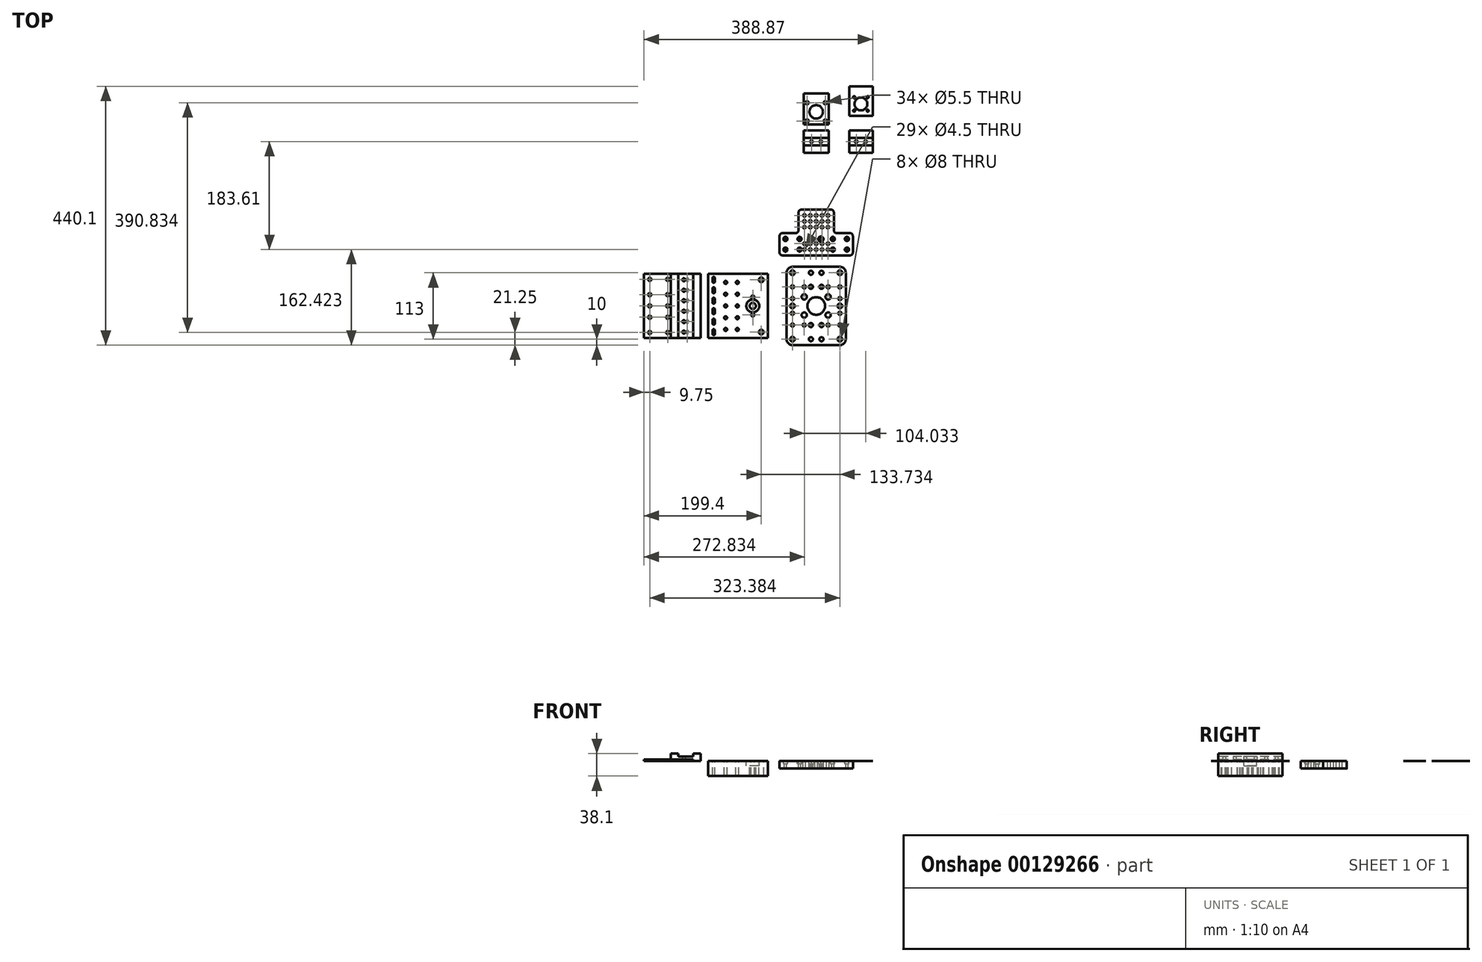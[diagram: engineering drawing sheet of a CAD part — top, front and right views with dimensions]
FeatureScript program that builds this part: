
annotation { "Feature Type Name" : "Feature", "Feature Type Description" : "" }
export const myFeature = defineFeature(function(context is Context, id is Id, definition is map)
    precondition{}
    {
        {
            var Q0;
            Q0=qCreatedBy(makeId("Top.planeOp"),FACE);
            var sketch = newSketch(context, id + "F0", { "sketchPlane" : qUnion([Q0])});
            skLineSegment(sketch, "E0.bottom", {"start": v(0, 0) * mm, "end": v(101.6, 0) * mm});
            skLineSegment(sketch, "E0.top", {"start": v(0, 109) * mm, "end": v(101.6, 109) * mm});
            skLineSegment(sketch, "E0.left", {"start": v(0, 0) * mm, "end": v(0, 109) * mm});
            skLineSegment(sketch, "E0.right", {"start": v(101.6, 0) * mm, "end": v(101.6, 109) * mm});
            skLineSegment(sketch, "E1", {"start": v(9.74, 0) * mm, "end": v(9.74, 109) * mm, "construction": true});
            skLineSegment(sketch, "E2", {"start": v(0, 10) * mm, "end": v(9.74, 10) * mm, "construction": true});
            skLineSegment(sketch, "E3.0.1.0", {"start": v(0, 27.8) * mm, "end": v(9.74, 27.8) * mm, "construction": true});
            skLineSegment(sketch, "E3.0.2.0", {"start": v(0, 45.6) * mm, "end": v(9.74, 45.6) * mm, "construction": true});
            skLineSegment(sketch, "E3.0.3.0", {"start": v(0, 63.4) * mm, "end": v(9.74, 63.4) * mm, "construction": true});
            skLineSegment(sketch, "E3.0.4.0", {"start": v(0, 81.2) * mm, "end": v(9.74, 81.2) * mm, "construction": true});
            skLineSegment(sketch, "E3.0.5.0", {"start": v(0, 99) * mm, "end": v(9.74, 99) * mm, "construction": true});
            skLineSegment(sketch, "E3.direction2", {"start": v(0, 10) * mm, "end": v(0, 27.8) * mm, "construction": true});
            skArc(sketch, "E4", {"start": v(11.74, 30.8) * mm, "mid": v(9.74, 32.8) * mm, "end": v(7.74, 30.8) * mm});
            skLineSegment(sketch, "E5", {"start": v(9.74, 30.8) * mm, "end": v(9.74, 24.8) * mm, "construction": true});
            skArc(sketch, "E6", {"start": v(7.74, 24.8) * mm, "mid": v(9.74, 22.8) * mm, "end": v(11.74, 24.8) * mm});
            skLineSegment(sketch, "E7", {"start": v(11.74, 30.8) * mm, "end": v(11.74, 24.8) * mm});
            skLineSegment(sketch, "E8", {"start": v(7.74, 24.8) * mm, "end": v(7.74, 30.8) * mm});
            skPoint(sketch, "E9", {"position": v(9.74, 27.8) * mm});
            skArc(sketch, "E10", {"start": v(11.74, 48.6) * mm, "mid": v(9.74, 50.6) * mm, "end": v(7.74, 48.6) * mm});
            skLineSegment(sketch, "E11", {"start": v(9.74, 48.6) * mm, "end": v(9.74, 42.6) * mm, "construction": true});
            skArc(sketch, "E12", {"start": v(7.74, 42.6) * mm, "mid": v(9.74, 40.6) * mm, "end": v(11.74, 42.6) * mm});
            skLineSegment(sketch, "E13", {"start": v(11.74, 48.6) * mm, "end": v(11.74, 42.6) * mm});
            skLineSegment(sketch, "E14", {"start": v(7.74, 42.6) * mm, "end": v(7.74, 48.6) * mm});
            skPoint(sketch, "E15", {"position": v(9.74, 45.6) * mm});
            skArc(sketch, "E16", {"start": v(11.74, 102) * mm, "mid": v(9.74, 104) * mm, "end": v(7.74, 102) * mm});
            skLineSegment(sketch, "E17", {"start": v(9.74, 102) * mm, "end": v(9.74, 96) * mm, "construction": true});
            skArc(sketch, "E18", {"start": v(7.74, 96) * mm, "mid": v(9.74, 94) * mm, "end": v(11.74, 96) * mm});
            skLineSegment(sketch, "E19", {"start": v(11.74, 102) * mm, "end": v(11.74, 96) * mm});
            skLineSegment(sketch, "E20", {"start": v(7.74, 96) * mm, "end": v(7.74, 102) * mm});
            skPoint(sketch, "E21", {"position": v(9.74, 99) * mm});
            skArc(sketch, "E22", {"start": v(11.74, 13) * mm, "mid": v(9.74, 15) * mm, "end": v(7.74, 13) * mm});
            skLineSegment(sketch, "E23", {"start": v(9.74, 13) * mm, "end": v(9.74, 7) * mm, "construction": true});
            skArc(sketch, "E24", {"start": v(7.74, 7) * mm, "mid": v(9.74, 5) * mm, "end": v(11.74, 7) * mm});
            skLineSegment(sketch, "E25", {"start": v(11.74, 13) * mm, "end": v(11.74, 7) * mm});
            skLineSegment(sketch, "E26", {"start": v(7.74, 7) * mm, "end": v(7.74, 13) * mm});
            skPoint(sketch, "E27", {"position": v(9.74, 10) * mm});
            skArc(sketch, "E28", {"start": v(11.74, 84.2) * mm, "mid": v(9.74, 86.2) * mm, "end": v(7.74, 84.2) * mm});
            skLineSegment(sketch, "E29", {"start": v(9.74, 84.2) * mm, "end": v(9.74, 78.2) * mm, "construction": true});
            skArc(sketch, "E30", {"start": v(7.74, 78.2) * mm, "mid": v(9.74, 76.2) * mm, "end": v(11.74, 78.2) * mm});
            skLineSegment(sketch, "E31", {"start": v(11.74, 84.2) * mm, "end": v(11.74, 78.2) * mm});
            skLineSegment(sketch, "E32", {"start": v(7.74, 78.2) * mm, "end": v(7.74, 84.2) * mm});
            skPoint(sketch, "E33", {"position": v(9.74, 81.2) * mm});
            skArc(sketch, "E34", {"start": v(11.74, 66.4) * mm, "mid": v(9.74, 68.4) * mm, "end": v(7.74, 66.4) * mm});
            skLineSegment(sketch, "E35", {"start": v(9.74, 66.4) * mm, "end": v(9.74, 60.4) * mm, "construction": true});
            skArc(sketch, "E36", {"start": v(7.74, 60.4) * mm, "mid": v(9.74, 58.4) * mm, "end": v(11.74, 60.4) * mm});
            skLineSegment(sketch, "E37", {"start": v(11.74, 66.4) * mm, "end": v(11.74, 60.4) * mm});
            skLineSegment(sketch, "E38", {"start": v(7.74, 60.4) * mm, "end": v(7.74, 66.4) * mm});
            skPoint(sketch, "E39", {"position": v(9.74, 63.4) * mm});
            skLineSegment(sketch, "E40", {"start": v(76.2, 109) * mm, "end": v(76.2, 0) * mm, "construction": true});
            skPoint(sketch, "E41", {"position": v(76.2, 69.5) * mm});
            skPoint(sketch, "E42", {"position": v(76.2, 54.5) * mm});
            skPoint(sketch, "E43", {"position": v(76.2, 39.5) * mm});
            skCircle(sketch, "E44", {"center": v(76.2, 69.5) * mm, "radius": 2.75 * mm});
            skCircle(sketch, "E45", {"center": v(76.2, 39.5) * mm, "radius": 2.75 * mm});
            skCircle(sketch, "E46", {"center": v(76.2, 54.5) * mm, "radius": 11 * mm});
            skCircle(sketch, "E47", {"center": v(76.2, 54.5) * mm, "radius": 5.26 * mm});
            skLineSegment(sketch, "E48", {"start": v(122.66, 27) * mm, "end": v(122.66, -7) * mm, "construction": true});
            skLineSegment(sketch, "E49", {"start": v(90.6, 10) * mm, "end": v(122.66, 10) * mm, "construction": true});
            skPoint(sketch, "E50", {"position": v(122.66, 10) * mm});
            skLineSegment(sketch, "E51", {"start": v(90.6, 99) * mm, "end": v(122.66, 99) * mm, "construction": true});
            skLineSegment(sketch, "E52", {"start": v(122.66, 116) * mm, "end": v(122.66, 82) * mm, "construction": true});
            skPoint(sketch, "E53", {"position": v(122.66, 99) * mm});
            skLineSegment(sketch, "E54", {"start": v(122.66, 54.5) * mm, "end": v(76.2, 54.5) * mm, "construction": true});
            skLineSegment(sketch, "E55", {"start": v(122.66, 74.5) * mm, "end": v(122.66, 34.5) * mm, "construction": true});
            skPoint(sketch, "E56", {"position": v(122.66, 54.5) * mm});
            skLineSegment(sketch, "E57", {"start": v(90.6, 109) * mm, "end": v(90.6, 0) * mm, "construction": true});
            skPoint(sketch, "E58", {"position": v(90.6, 99) * mm});
            skPoint(sketch, "E59", {"position": v(90.6, 10) * mm});
            skLineSegment(sketch, "E60", {"start": v(122.66, 82) * mm, "end": v(122.66, 74.5) * mm, "construction": true});
            skLineSegment(sketch, "E61", {"start": v(122.66, 34.5) * mm, "end": v(122.66, 27) * mm, "construction": true});
            skCircle(sketch, "E62", {"center": v(90.6, 99) * mm, "radius": 4 * mm});
            skCircle(sketch, "E63", {"center": v(90.6, 10) * mm, "radius": 4 * mm});
            skLineSegment(sketch, "E64", {"start": v(30, 109) * mm, "end": v(30, 0) * mm, "construction": true});
            skLineSegment(sketch, "E65", {"start": v(50, 109) * mm, "end": v(50, 0) * mm, "construction": true});
            skLineSegment(sketch, "E66", {"start": v(50, 54.5) * mm, "end": v(30, 54.5) * mm, "construction": true});
            skLineSegment(sketch, "E67", {"start": v(30, 74.5) * mm, "end": v(50, 74.5) * mm, "construction": true});
            skLineSegment(sketch, "E68", {"start": v(50, 94.5) * mm, "end": v(30, 94.5) * mm, "construction": true});
            skLineSegment(sketch, "E69", {"start": v(30, 34.5) * mm, "end": v(50, 34.5) * mm, "construction": true});
            skLineSegment(sketch, "E70", {"start": v(50, 14.5) * mm, "end": v(30, 14.5) * mm, "construction": true});
            skCircle(sketch, "E71", {"center": v(30, 94.5) * mm, "radius": 2.55 * mm});
            skCircle(sketch, "E72", {"center": v(50, 94.5) * mm, "radius": 2.55 * mm});
            skCircle(sketch, "E73", {"center": v(30, 74.5) * mm, "radius": 2.55 * mm});
            skCircle(sketch, "E74", {"center": v(50, 74.5) * mm, "radius": 2.55 * mm});
            skCircle(sketch, "E75", {"center": v(50, 54.5) * mm, "radius": 2.55 * mm});
            skCircle(sketch, "E76", {"center": v(30, 54.5) * mm, "radius": 2.55 * mm});
            skCircle(sketch, "E77", {"center": v(30, 34.5) * mm, "radius": 2.55 * mm});
            skCircle(sketch, "E78", {"center": v(50, 34.5) * mm, "radius": 2.55 * mm});
            skCircle(sketch, "E79", {"center": v(50, 14.5) * mm, "radius": 2.55 * mm});
            skCircle(sketch, "E80", {"center": v(30, 14.5) * mm, "radius": 2.55 * mm});
            skLineSegment(sketch, "E81", {"start": v(101.6, 116.15) * mm, "end": v(101.6, 102.86) * mm});
            skLineSegment(sketch, "E82", {"start": v(76.2, 85.11) * mm, "end": v(94.2, 85.11) * mm});
            skSolve(sketch);
        }
        {
            var Q0;
            Q0=qCreatedBy(makeId("Top.planeOp"),FACE);
            var sketch = newSketch(context, id + "F1", { "sketchPlane" : qUnion([Q0])});
            skLineSegment(sketch, "E83.bottom", {"start": v(-25.4, 0) * mm, "end": v(-50.8, 0) * mm});
            skLineSegment(sketch, "E83.top", {"start": v(-25.4, 109) * mm, "end": v(-50.8, 109) * mm});
            skLineSegment(sketch, "E83.left", {"start": v(-25.4, 0) * mm, "end": v(-25.4, 109) * mm, "construction": true});
            skLineSegment(sketch, "E83.right", {"start": v(-50.8, 0) * mm, "end": v(-50.8, 109) * mm, "construction": true});
            skLineSegment(sketch, "E84", {"start": v(0, 0) * mm, "end": v(-25.4, 0) * mm, "construction": true});
            skLineSegment(sketch, "E85", {"start": v(-25.4, 109) * mm, "end": v(0, 109) * mm, "construction": true});
            skLineSegment(sketch, "E86", {"start": v(-50.8, 99) * mm, "end": v(0, 99) * mm, "construction": true});
            skLineSegment(sketch, "E87", {"start": v(-50.8, 81.2) * mm, "end": v(0, 81.2) * mm, "construction": true});
            skLineSegment(sketch, "E88", {"start": v(-50.8, 63.4) * mm, "end": v(0, 63.4) * mm, "construction": true});
            skLineSegment(sketch, "E89", {"start": v(-50.8, 45.6) * mm, "end": v(0, 45.6) * mm, "construction": true});
            skLineSegment(sketch, "E90", {"start": v(-50.8, 27.8) * mm, "end": v(0, 27.8) * mm, "construction": true});
            skLineSegment(sketch, "E91", {"start": v(-50.8, 10) * mm, "end": v(0, 10) * mm, "construction": true});
            skLineSegment(sketch, "E92", {"start": v(-41.06, 109) * mm, "end": v(-41.06, 0) * mm, "construction": true});
            skCircle(sketch, "E93", {"center": v(-41.06, 99) * mm, "radius": 2.5 * mm});
            skCircle(sketch, "E94", {"center": v(-41.06, 81.2) * mm, "radius": 2.5 * mm});
            skCircle(sketch, "E95", {"center": v(-41.06, 63.4) * mm, "radius": 2.5 * mm});
            skCircle(sketch, "E96", {"center": v(-41.06, 45.6) * mm, "radius": 2.5 * mm});
            skCircle(sketch, "E97", {"center": v(-41.06, 27.8) * mm, "radius": 2.5 * mm});
            skCircle(sketch, "E98", {"center": v(-41.06, 10) * mm, "radius": 2.5 * mm});
            skLineSegment(sketch, "E99", {"start": v(-50.8, 109) * mm, "end": v(-63.5, 109) * mm});
            skLineSegment(sketch, "E100", {"start": v(-63.5, 109) * mm, "end": v(-63.5, 0) * mm});
            skLineSegment(sketch, "E101", {"start": v(-63.5, 0) * mm, "end": v(-50.8, 0) * mm});
            skLineSegment(sketch, "E102", {"start": v(-25.4, 0) * mm, "end": v(-12.7, 0) * mm});
            skPoint(sketch, "E102.endSnap0", {"position": v(-12.7, 0) * mm});
            skLineSegment(sketch, "E103", {"start": v(-12.7, 0) * mm, "end": v(-12.7, 109) * mm});
            skLineSegment(sketch, "E104", {"start": v(-12.7, 109) * mm, "end": v(-25.4, 109) * mm});
            skSolve(sketch);
        }
        {
            var Q0;
            Q0=makeQuery(id+"F1.imprint","IMPRINT",FACE,{"disambiguationData":[TD([[makeQuery(id+"F1.imprint","IMPRINT",EDGE,{"derivedFrom":sQuery(id+"F1.wireOp",EDGE,"E83.bottom")}),-1.0]])]});
            extrude(context, id + "F2", {"entities" : qUnion([Q0]), "depth" : 12.7 * mm});
        }
        {
            var Q0;
            Q0=makeQuery(id+"F2.opExtrude","CAP_FACE",FACE,{"disambiguationData":[OSD([sQuery(id+"F1.wireOp",EDGE,"E83.bottom"),sQuery(id+"F1.wireOp",EDGE,"E83.top"),sQuery(id+"F1.wireOp",EDGE,"E93"),sQuery(id+"F1.wireOp",EDGE,"E94"),sQuery(id+"F1.wireOp",EDGE,"E95"),sQuery(id+"F1.wireOp",EDGE,"E96"),sQuery(id+"F1.wireOp",EDGE,"E97"),sQuery(id+"F1.wireOp",EDGE,"E98"),sQuery(id+"F1.wireOp",EDGE,"E99"),sQuery(id+"F1.wireOp",EDGE,"E100"),sQuery(id+"F1.wireOp",EDGE,"E101"),sQuery(id+"F1.wireOp",EDGE,"E102"),sQuery(id+"F1.wireOp",EDGE,"E103"),sQuery(id+"F1.wireOp",EDGE,"E104")])],"isStart":false});
            var sketch = newSketch(context, id + "F3", { "sketchPlane" : qUnion([Q0])});
            skLineSegment(sketch, "E105", {"start": v(-50.8, 109) * mm, "end": v(-50.8, 0) * mm});
            skLineSegment(sketch, "E106", {"start": v(-25.4, 109) * mm, "end": v(-25.4, 0) * mm});
            skSolve(sketch);
        }
        {
            var Q0;
            {var subQ0=sQuery(id+"F3.wireOp",EDGE,"E105");Q0=makeQuery(id+"F3.imprint","IMPRINT",FACE,{"disambiguationData":[TD([[makeQuery(id+"F3.imprint","IMPRINT",EDGE,{"derivedFrom":subQ0}),1.0]])]});}
            extrude(context, id + "F4", {"entities" : qUnion([Q0]), "operationType" : NewBodyOperationType.REMOVE, "oppositeDirection" : true, "depth" : 5 * mm});
        }
        {
            var Q0;
            Q0=makeQuery(id+"F0.imprint","IMPRINT",FACE,{"disambiguationData":[TD([[makeQuery(id+"F0.imprint","IMPRINT",EDGE,{"derivedFrom":sQuery(id+"F0.wireOp",EDGE,"E46")}),1.0]])]});
            var Q1;
            Q1=makeQuery(id+"F0.imprint","IMPRINT",FACE,{"disambiguationData":[TD([[makeQuery(id+"F0.imprint","IMPRINT",EDGE,{"derivedFrom":sQuery(id+"F0.wireOp",EDGE,"E0.bottom")}),1.0]])]});
            extrude(context, id + "F5", {"entities" : qUnion([Q0, Q1]), "oppositeDirection" : true, "depth" : 25.4 * mm});
        }
        {
            var Q0;
            Q0=makeQuery(id+"F0.imprint","IMPRINT",FACE,{"disambiguationData":[TD([[makeQuery(id+"F0.imprint","IMPRINT",EDGE,{"derivedFrom":sQuery(id+"F0.wireOp",EDGE,"E46")}),1.0]])]});
            extrude(context, id + "F6", {"entities" : qUnion([Q0]), "operationType" : NewBodyOperationType.REMOVE, "oppositeDirection" : true, "depth" : 8 * mm});
        }
        {
            var Q0;
            Q0=makeQuery(id+"F0.imprint","IMPRINT",FACE,{"disambiguationData":[TD([[makeQuery(id+"F0.imprint","IMPRINT",EDGE,{"derivedFrom":sQuery(id+"F0.wireOp",EDGE,"E0.bottom")}),1.0]])]});
            var sketch = newSketch(context, id + "F7", { "sketchPlane" : qUnion([Q0])});
            skLineSegment(sketch, "E107.bottom", {"start": v(-25.4, 109) * mm, "end": v(-58.8, 109) * mm});
            skLineSegment(sketch, "E107.top", {"start": v(-25.4, 0) * mm, "end": v(-108.8, 0) * mm});
            skLineSegment(sketch, "E107.left", {"start": v(-25.4, 109) * mm, "end": v(-25.4, 0) * mm});
            skLineSegment(sketch, "E107.right", {"start": v(-108.8, 109) * mm, "end": v(-108.8, 0) * mm});
            skLineSegment(sketch, "E108", {"start": v(0, 109) * mm, "end": v(-25.4, 109) * mm, "construction": true});
            skLineSegment(sketch, "E109", {"start": v(0, 0) * mm, "end": v(-25.4, 0) * mm, "construction": true});
            skLineSegment(sketch, "E110", {"start": v(-58.8, 109) * mm, "end": v(-58.8, 54.5) * mm, "construction": true});
            skLineSegment(sketch, "E111", {"start": v(-35.14, 109) * mm, "end": v(-35.14, 0) * mm, "construction": true});
            skLineSegment(sketch, "E112", {"start": v(-35.14, 99) * mm, "end": v(0, 99) * mm, "construction": true});
            skLineSegment(sketch, "E113", {"start": v(-35.14, 81.2) * mm, "end": v(0, 81.2) * mm, "construction": true});
            skLineSegment(sketch, "E114", {"start": v(-35.14, 63.4) * mm, "end": v(0, 63.4) * mm, "construction": true});
            skLineSegment(sketch, "E115", {"start": v(-35.14, 45.6) * mm, "end": v(0, 45.6) * mm, "construction": true});
            skLineSegment(sketch, "E116", {"start": v(-35.14, 27.8) * mm, "end": v(0, 27.8) * mm, "construction": true});
            skLineSegment(sketch, "E117", {"start": v(-35.14, 10) * mm, "end": v(0, 10) * mm, "construction": true});
            skPoint(sketch, "E118", {"position": v(9.74, 109) * mm});
            skLineSegment(sketch, "E119", {"start": v(0, 109) * mm, "end": v(9.74, 109) * mm, "construction": true});
            skLineSegment(sketch, "E120", {"start": v(-25.4, 109) * mm, "end": v(-35.14, 109) * mm, "construction": true});
            skCircle(sketch, "E121", {"center": v(-35.14, 99) * mm, "radius": 2.75 * mm});
            skCircle(sketch, "E122", {"center": v(-35.14, 81.2) * mm, "radius": 2.75 * mm});
            skCircle(sketch, "E123", {"center": v(-35.14, 63.4) * mm, "radius": 2.75 * mm});
            skCircle(sketch, "E124", {"center": v(-35.14, 45.6) * mm, "radius": 2.75 * mm});
            skCircle(sketch, "E125", {"center": v(-35.14, 27.8) * mm, "radius": 2.75 * mm});
            skCircle(sketch, "E126", {"center": v(-35.14, 10) * mm, "radius": 2.75 * mm});
            skLineSegment(sketch, "E127", {"start": v(-58.8, 54.5) * mm, "end": v(-108.8, 54.5) * mm, "construction": true});
            skLineSegment(sketch, "E128", {"start": v(-58.8, 109) * mm, "end": v(-83.8, 109) * mm});
            skLineSegment(sketch, "E129", {"start": v(-58.8, 54.5) * mm, "end": v(-58.8, 0) * mm, "construction": true});
            skLineSegment(sketch, "E130", {"start": v(-83.8, 109) * mm, "end": v(-83.8, 0) * mm, "construction": true});
            skLineSegment(sketch, "E131", {"start": v(-99.05, 109) * mm, "end": v(-99.05, 0) * mm, "construction": true});
            skLineSegment(sketch, "E132", {"start": v(-68.55, 109) * mm, "end": v(-68.55, 0) * mm, "construction": true});
            skLineSegment(sketch, "E133", {"start": v(-83.8, 109) * mm, "end": v(-108.8, 109) * mm});
            skLineSegment(sketch, "E134", {"start": v(-50.8, 109) * mm, "end": v(-50.8, 0) * mm, "construction": true});
            skLineSegment(sketch, "E135", {"start": v(-108.8, 64.5) * mm, "end": v(-58.8, 64.5) * mm, "construction": true});
            skLineSegment(sketch, "E136", {"start": v(-108.8, 44.5) * mm, "end": v(-58.8, 44.5) * mm, "construction": true});
            skLineSegment(sketch, "E137", {"start": v(-108.8, 86.75) * mm, "end": v(-58.8, 86.75) * mm, "construction": true});
            skLineSegment(sketch, "E138", {"start": v(-108.8, 99.75) * mm, "end": v(-58.8, 99.75) * mm, "construction": true});
            skLineSegment(sketch, "E139", {"start": v(-108.8, 73.75) * mm, "end": v(-58.8, 73.75) * mm, "construction": true});
            skLineSegment(sketch, "E140", {"start": v(-108.8, 22.25) * mm, "end": v(-58.8, 22.25) * mm, "construction": true});
            skLineSegment(sketch, "E141", {"start": v(-108.8, 35.25) * mm, "end": v(-58.8, 35.25) * mm, "construction": true});
            skLineSegment(sketch, "E142", {"start": v(-58.8, 9.25) * mm, "end": v(-108.8, 9.25) * mm, "construction": true});
            skCircle(sketch, "E143", {"center": v(-99.05, 99.75) * mm, "radius": 2.75 * mm});
            skCircle(sketch, "E144", {"center": v(-68.55, 99.75) * mm, "radius": 2.75 * mm});
            skCircle(sketch, "E145", {"center": v(-68.55, 73.75) * mm, "radius": 2.75 * mm});
            skCircle(sketch, "E146", {"center": v(-99.05, 73.75) * mm, "radius": 2.75 * mm});
            skCircle(sketch, "E147", {"center": v(-99.05, 35.25) * mm, "radius": 2.75 * mm});
            skCircle(sketch, "E148", {"center": v(-99.05, 9.25) * mm, "radius": 2.75 * mm});
            skCircle(sketch, "E149", {"center": v(-68.55, 9.25) * mm, "radius": 2.75 * mm});
            skCircle(sketch, "E150", {"center": v(-68.55, 35.25) * mm, "radius": 2.75 * mm});
            skCircle(sketch, "E151", {"center": v(-68.55, 54.5) * mm, "radius": 2.75 * mm});
            skCircle(sketch, "E152", {"center": v(-99.05, 54.5) * mm, "radius": 2.75 * mm});
            skSolve(sketch);
        }
        {
            var Q0;
            Q0=makeQuery(id+"F7.imprint","IMPRINT",FACE,{"disambiguationData":[TD([[makeQuery(id+"F7.imprint","IMPRINT",EDGE,{"derivedFrom":sQuery(id+"F7.wireOp",EDGE,"E107.bottom")}),1.0]])]});
            extrude(context, id + "F8", {"entities" : qUnion([Q0]), "depth" : 3 * mm});
        }
        {
            var Q0;
            Q0=makeQuery(id+"F0.imprint","IMPRINT",FACE,{"disambiguationData":[TD([[makeQuery(id+"F0.imprint","IMPRINT",EDGE,{"derivedFrom":sQuery(id+"F0.wireOp",EDGE,"E0.bottom")}),1.0]])]});
            var sketch = newSketch(context, id + "F9", { "sketchPlane" : qUnion([Q0])});
            skLineSegment(sketch, "E153.bottom", {"start": v(143.73, -12) * mm, "end": v(224.33, -12) * mm});
            skLineSegment(sketch, "E153.top", {"start": v(143.73, 121) * mm, "end": v(224.33, 121) * mm});
            skLineSegment(sketch, "E153.left", {"start": v(224.33, 121) * mm, "end": v(224.33, -12) * mm, "construction": true});
            skLineSegment(sketch, "E153.right", {"start": v(143.73, 121) * mm, "end": v(143.73, -12) * mm, "construction": true});
            skLineSegment(sketch, "E154", {"start": v(143.73, 10) * mm, "end": v(122.66, 10) * mm, "construction": true});
            skLineSegment(sketch, "E155", {"start": v(143.73, 99) * mm, "end": v(122.66, 99) * mm, "construction": true});
            skLineSegment(sketch, "E156", {"start": v(184.03, 121) * mm, "end": v(184.03, -12) * mm, "construction": true});
            skLineSegment(sketch, "E157", {"start": v(122.66, 54.5) * mm, "end": v(143.73, 54.5) * mm, "construction": true});
            skLineSegment(sketch, "E158", {"start": v(193.03, 111) * mm, "end": v(193.03, 87) * mm, "construction": true});
            skPoint(sketch, "E159", {"position": v(193.03, 99) * mm});
            skLineSegment(sketch, "E160", {"start": v(193.03, 87) * mm, "end": v(175.03, 87) * mm, "construction": true});
            skPoint(sketch, "E161", {"position": v(184.03, 87) * mm});
            skLineSegment(sketch, "E162", {"start": v(193.03, 111) * mm, "end": v(175.03, 111) * mm, "construction": true});
            skLineSegment(sketch, "E163", {"start": v(175.03, 87) * mm, "end": v(175.03, 111) * mm, "construction": true});
            skLineSegment(sketch, "E164", {"start": v(193.03, 22) * mm, "end": v(193.03, -2) * mm, "construction": true});
            skPoint(sketch, "E165", {"position": v(193.03, 10) * mm});
            skLineSegment(sketch, "E166", {"start": v(193.03, 22) * mm, "end": v(175.03, 22) * mm, "construction": true});
            skPoint(sketch, "E167", {"position": v(184.03, 22) * mm});
            skLineSegment(sketch, "E168", {"start": v(175.03, 22) * mm, "end": v(175.03, -2) * mm, "construction": true});
            skLineSegment(sketch, "E169", {"start": v(175.03, -2) * mm, "end": v(193.03, -2) * mm, "construction": true});
            skLineSegment(sketch, "E170", {"start": v(204.33, 39) * mm, "end": v(163.73, 39) * mm, "construction": true});
            skPoint(sketch, "E171", {"position": v(184.03, 39) * mm});
            skLineSegment(sketch, "E172", {"start": v(163.73, 39) * mm, "end": v(163.73, 70) * mm, "construction": true});
            skLineSegment(sketch, "E173", {"start": v(163.73, 70) * mm, "end": v(204.33, 70) * mm, "construction": true});
            skCircle(sketch, "E174", {"center": v(175.03, 111) * mm, "radius": 2.25 * mm});
            skCircle(sketch, "E175", {"center": v(193.03, 87) * mm, "radius": 2.25 * mm});
            skCircle(sketch, "E176", {"center": v(175.03, 87) * mm, "radius": 2.25 * mm});
            skCircle(sketch, "E177", {"center": v(193.03, 111) * mm, "radius": 2.25 * mm});
            skCircle(sketch, "E178", {"center": v(193.03, 22) * mm, "radius": 2.25 * mm});
            skCircle(sketch, "E179", {"center": v(193.03, -2) * mm, "radius": 2.25 * mm});
            skCircle(sketch, "E180", {"center": v(175.03, 22) * mm, "radius": 2.25 * mm});
            skCircle(sketch, "E181", {"center": v(175.03, -2) * mm, "radius": 2.25 * mm});
            skCircle(sketch, "E182", {"center": v(163.73, 39) * mm, "radius": 2.75 * mm});
            skCircle(sketch, "E183", {"center": v(204.33, 70) * mm, "radius": 2.75 * mm});
            skCircle(sketch, "E184", {"center": v(163.73, 70) * mm, "radius": 2.75 * mm});
            skCircle(sketch, "E185", {"center": v(204.33, 39) * mm, "radius": 2.75 * mm});
            skLineSegment(sketch, "E186", {"start": v(204.33, 39) * mm, "end": v(204.33, 70) * mm, "construction": true});
            skPoint(sketch, "E187", {"position": v(163.73, 54.5) * mm});
            skLineSegment(sketch, "E188", {"start": v(163.73, 54.5) * mm, "end": v(143.73, 54.5) * mm, "construction": true});
            skLineSegment(sketch, "E189", {"start": v(143.73, 121) * mm, "end": v(143.73, 121) * mm});
            skLineSegment(sketch, "E190", {"start": v(133.73, 111) * mm, "end": v(133.73, -2) * mm});
            skLineSegment(sketch, "E191", {"start": v(143.73, -12) * mm, "end": v(143.73, -12) * mm});
            skLineSegment(sketch, "E192", {"start": v(224.33, -12) * mm, "end": v(224.33, -12) * mm});
            skLineSegment(sketch, "E193", {"start": v(234.33, -2) * mm, "end": v(234.33, 111) * mm});
            skLineSegment(sketch, "E194", {"start": v(224.33, 121) * mm, "end": v(224.33, 121) * mm});
            skPoint(sketch, "E195.visualSharp", {"position": v(133.73, 121) * mm});
            skArc(sketch, "E195.filletArc", {"start": v(143.73, 121) * mm, "mid": v(136.66, 118.07) * mm, "end": v(133.73, 111) * mm});
            skPoint(sketch, "E196.visualSharp", {"position": v(133.73, -12) * mm});
            skArc(sketch, "E196.filletArc", {"start": v(133.73, -2) * mm, "mid": v(136.66, -9.07) * mm, "end": v(143.73, -12) * mm});
            skCircle(sketch, "E197", {"center": v(143.73, 111) * mm, "radius": 4 * mm});
            skPoint(sketch, "E198.visualSharp", {"position": v(234.33, 121) * mm});
            skArc(sketch, "E198.filletArc", {"start": v(234.33, 111) * mm, "mid": v(231.4, 118.07) * mm, "end": v(224.33, 121) * mm});
            skPoint(sketch, "E199.visualSharp", {"position": v(234.33, -12) * mm});
            skArc(sketch, "E199.filletArc", {"start": v(224.33, -12) * mm, "mid": v(231.4, -9.07) * mm, "end": v(234.33, -2) * mm});
            skCircle(sketch, "E200", {"center": v(224.33, 111) * mm, "radius": 4 * mm});
            skCircle(sketch, "E201", {"center": v(163.73, 70) * mm, "radius": 4.5 * mm});
            skCircle(sketch, "E202", {"center": v(204.33, 70) * mm, "radius": 4.5 * mm});
            skCircle(sketch, "E203", {"center": v(163.73, 39) * mm, "radius": 4.5 * mm});
            skCircle(sketch, "E204", {"center": v(204.33, 39) * mm, "radius": 4.5 * mm});
            skCircle(sketch, "E205", {"center": v(175.03, 111) * mm, "radius": 3.5 * mm});
            skCircle(sketch, "E206", {"center": v(175.03, 87) * mm, "radius": 3.5 * mm});
            skCircle(sketch, "E207", {"center": v(193.03, 111) * mm, "radius": 3.5 * mm});
            skCircle(sketch, "E208", {"center": v(193.03, 87) * mm, "radius": 3.5 * mm});
            skCircle(sketch, "E209", {"center": v(175.03, 22) * mm, "radius": 3.5 * mm});
            skCircle(sketch, "E210", {"center": v(175.03, -2) * mm, "radius": 3.5 * mm});
            skCircle(sketch, "E211", {"center": v(193.03, 22) * mm, "radius": 3.5 * mm});
            skCircle(sketch, "E212", {"center": v(193.03, -2) * mm, "radius": 3.5 * mm});
            skLineSegment(sketch, "E213", {"start": v(156.23, 77.5) * mm, "end": v(211.83, 77.5) * mm, "construction": true});
            skPoint(sketch, "E214", {"position": v(184.03, 77.5) * mm});
            skLineSegment(sketch, "E215", {"start": v(156.23, 77.5) * mm, "end": v(156.23, 31.5) * mm, "construction": true});
            skPoint(sketch, "E216", {"position": v(156.23, 54.5) * mm});
            skLineSegment(sketch, "E217", {"start": v(156.23, 31.5) * mm, "end": v(211.83, 31.5) * mm, "construction": true});
            skLineSegment(sketch, "E218", {"start": v(211.83, 77.5) * mm, "end": v(211.83, 31.5) * mm, "construction": true});
            skLineSegment(sketch, "E219.bottom", {"start": v(169.03, 116) * mm, "end": v(199.03, 116) * mm, "construction": true});
            skLineSegment(sketch, "E219.top", {"start": v(169.03, 82) * mm, "end": v(199.03, 82) * mm, "construction": true});
            skLineSegment(sketch, "E219.left", {"start": v(169.03, 116) * mm, "end": v(169.03, 82) * mm, "construction": true});
            skLineSegment(sketch, "E219.right", {"start": v(199.03, 116) * mm, "end": v(199.03, 82) * mm, "construction": true});
            skPoint(sketch, "E220", {"position": v(184.03, 116) * mm});
            skPoint(sketch, "E221", {"position": v(169.03, 99) * mm});
            skLineSegment(sketch, "E222.bottom", {"start": v(160.73, 100) * mm, "end": v(126.73, 100) * mm, "construction": true});
            skLineSegment(sketch, "E222.top", {"start": v(160.73, 122) * mm, "end": v(126.73, 122) * mm, "construction": true});
            skLineSegment(sketch, "E222.left", {"start": v(160.73, 100) * mm, "end": v(160.73, 122) * mm, "construction": true});
            skLineSegment(sketch, "E222.right", {"start": v(126.73, 100) * mm, "end": v(126.73, 122) * mm, "construction": true});
            skLineSegment(sketch, "E223", {"start": v(175.03, 87) * mm, "end": v(163.73, 87) * mm, "construction": true});
            skLineSegment(sketch, "E224", {"start": v(163.73, 87) * mm, "end": v(163.73, 70) * mm, "construction": true});
            skLineSegment(sketch, "E225", {"start": v(193.03, 87) * mm, "end": v(204.33, 87) * mm, "construction": true});
            skLineSegment(sketch, "E226", {"start": v(204.33, 87) * mm, "end": v(204.33, 70) * mm, "construction": true});
            skLineSegment(sketch, "E227", {"start": v(204.33, 87) * mm, "end": v(224.33, 87) * mm, "construction": true});
            skLineSegment(sketch, "E228", {"start": v(163.73, 87) * mm, "end": v(143.73, 87) * mm, "construction": true});
            skCircle(sketch, "E229", {"center": v(163.73, 87) * mm, "radius": 2.75 * mm});
            skCircle(sketch, "E230", {"center": v(204.33, 87) * mm, "radius": 2.75 * mm});
            skCircle(sketch, "E231", {"center": v(163.73, 87) * mm, "radius": 4.5 * mm, "construction": true});
            skLineSegment(sketch, "E232", {"start": v(175.03, 22) * mm, "end": v(163.73, 22) * mm, "construction": true});
            skLineSegment(sketch, "E233", {"start": v(163.73, 22) * mm, "end": v(163.73, 39) * mm, "construction": true});
            skLineSegment(sketch, "E234", {"start": v(163.73, 22) * mm, "end": v(143.73, 22) * mm, "construction": true});
            skLineSegment(sketch, "E235", {"start": v(204.33, 39) * mm, "end": v(204.33, 22) * mm, "construction": true});
            skLineSegment(sketch, "E236", {"start": v(204.33, 22) * mm, "end": v(193.03, 22) * mm, "construction": true});
            skLineSegment(sketch, "E237", {"start": v(204.33, 22) * mm, "end": v(224.33, 22) * mm, "construction": true});
            skCircle(sketch, "E238", {"center": v(163.73, 22) * mm, "radius": 2.75 * mm});
            skCircle(sketch, "E239", {"center": v(204.33, 22) * mm, "radius": 2.75 * mm});
            skCircle(sketch, "E240", {"center": v(143.73, -2) * mm, "radius": 4 * mm});
            skCircle(sketch, "E241", {"center": v(224.33, -2) * mm, "radius": 4 * mm});
            skCircle(sketch, "E242", {"center": v(143.73, 87) * mm, "radius": 2.75 * mm});
            skCircle(sketch, "E243", {"center": v(143.73, 22) * mm, "radius": 2.75 * mm});
            skCircle(sketch, "E244", {"center": v(224.33, 22) * mm, "radius": 2.75 * mm});
            skCircle(sketch, "E245", {"center": v(224.33, 42) * mm, "radius": 2.75 * mm});
            skCircle(sketch, "E246", {"center": v(224.33, 67) * mm, "radius": 2.75 * mm});
            skCircle(sketch, "E247", {"center": v(143.73, 67) * mm, "radius": 2.75 * mm});
            skCircle(sketch, "E248", {"center": v(143.73, 42) * mm, "radius": 2.75 * mm});
            skCircle(sketch, "E249", {"center": v(224.33, 87) * mm, "radius": 2.75 * mm});
            skCircle(sketch, "E250", {"center": v(143.73, 54.5) * mm, "radius": 4 * mm});
            skCircle(sketch, "E251", {"center": v(224.33, 54.5) * mm, "radius": 4 * mm});
            skLineSegment(sketch, "E252", {"start": v(143.73, 111) * mm, "end": v(175.03, 111) * mm, "construction": true});
            skLineSegment(sketch, "E253", {"start": v(224.33, 111) * mm, "end": v(193.03, 111) * mm, "construction": true});
            skCircle(sketch, "E254", {"center": v(153.73, 111) * mm, "radius": 3.18 * mm, "construction": true});
            skCircle(sketch, "E255", {"center": v(214.33, 111) * mm, "radius": 3.18 * mm, "construction": true});
            skCircle(sketch, "E256", {"center": v(143.73, 101) * mm, "radius": 3.18 * mm, "construction": true});
            skCircle(sketch, "E257", {"center": v(224.33, 101) * mm, "radius": 3.18 * mm, "construction": true});
            skLineSegment(sketch, "E258", {"start": v(143.73, -2) * mm, "end": v(175.03, -2) * mm, "construction": true});
            skLineSegment(sketch, "E259", {"start": v(193.03, -2) * mm, "end": v(224.33, -2) * mm, "construction": true});
            skCircle(sketch, "E260", {"center": v(143.73, 8) * mm, "radius": 3.18 * mm, "construction": true});
            skCircle(sketch, "E261", {"center": v(153.73, -2) * mm, "radius": 3.18 * mm, "construction": true});
            skCircle(sketch, "E262", {"center": v(214.33, -2) * mm, "radius": 3.18 * mm, "construction": true});
            skCircle(sketch, "E263", {"center": v(224.33, 8) * mm, "radius": 3.18 * mm, "construction": true});
            skCircle(sketch, "E264", {"center": v(184.03, 54.5) * mm, "radius": 15 * mm});
            skSolve(sketch);
        }
        {
            var Q0;
            Q0=makeQuery(id+"F9.imprint","IMPRINT",FACE,{"disambiguationData":[TD([[makeQuery(id+"F9.imprint","IMPRINT",EDGE,{"derivedFrom":sQuery(id+"F9.wireOp",EDGE,"E153.bottom")}),-1.0]])]});
            var Q1;
            Q1=makeQuery(id+"F9.imprint","IMPRINT",FACE,{"disambiguationData":[TD([[makeQuery(id+"F9.imprint","IMPRINT",EDGE,{"derivedFrom":sQuery(id+"F9.wireOp",EDGE,"E153.bottom")}),1.0]])]});
            var Q2;
            Q2=makeQuery(id+"F9.imprint","IMPRINT",FACE,{"disambiguationData":[TD([[makeQuery(id+"F9.imprint","IMPRINT",EDGE,{"derivedFrom":sQuery(id+"F9.wireOp",EDGE,"E174")}),-1.0]])]});
            var Q3;
            Q3=makeQuery(id+"F9.imprint","IMPRINT",FACE,{"disambiguationData":[TD([[makeQuery(id+"F9.imprint","IMPRINT",EDGE,{"derivedFrom":sQuery(id+"F9.wireOp",EDGE,"E176")}),-1.0]])]});
            var Q4;
            Q4=makeQuery(id+"F9.imprint","IMPRINT",FACE,{"disambiguationData":[TD([[makeQuery(id+"F9.imprint","IMPRINT",EDGE,{"derivedFrom":sQuery(id+"F9.wireOp",EDGE,"E175")}),-1.0]])]});
            var Q5;
            Q5=makeQuery(id+"F9.imprint","IMPRINT",FACE,{"disambiguationData":[TD([[makeQuery(id+"F9.imprint","IMPRINT",EDGE,{"derivedFrom":sQuery(id+"F9.wireOp",EDGE,"E177")}),-1.0]])]});
            var Q6;
            Q6=makeQuery(id+"F9.imprint","IMPRINT",FACE,{"disambiguationData":[TD([[makeQuery(id+"F9.imprint","IMPRINT",EDGE,{"derivedFrom":sQuery(id+"F9.wireOp",EDGE,"E184")}),-1.0]])]});
            var Q7;
            Q7=makeQuery(id+"F9.imprint","IMPRINT",FACE,{"disambiguationData":[TD([[makeQuery(id+"F9.imprint","IMPRINT",EDGE,{"derivedFrom":sQuery(id+"F9.wireOp",EDGE,"E182")}),-1.0]])]});
            var Q8;
            Q8=makeQuery(id+"F9.imprint","IMPRINT",FACE,{"disambiguationData":[TD([[makeQuery(id+"F9.imprint","IMPRINT",EDGE,{"derivedFrom":sQuery(id+"F9.wireOp",EDGE,"E185")}),-1.0]])]});
            var Q9;
            Q9=makeQuery(id+"F9.imprint","IMPRINT",FACE,{"disambiguationData":[TD([[makeQuery(id+"F9.imprint","IMPRINT",EDGE,{"derivedFrom":sQuery(id+"F9.wireOp",EDGE,"E183")}),-1.0]])]});
            var Q10;
            Q10=makeQuery(id+"F9.imprint","IMPRINT",FACE,{"disambiguationData":[TD([[makeQuery(id+"F9.imprint","IMPRINT",EDGE,{"derivedFrom":sQuery(id+"F9.wireOp",EDGE,"E180")}),-1.0]])]});
            var Q11;
            Q11=makeQuery(id+"F9.imprint","IMPRINT",FACE,{"disambiguationData":[TD([[makeQuery(id+"F9.imprint","IMPRINT",EDGE,{"derivedFrom":sQuery(id+"F9.wireOp",EDGE,"E181")}),-1.0]])]});
            var Q12;
            Q12=makeQuery(id+"F9.imprint","IMPRINT",FACE,{"disambiguationData":[TD([[makeQuery(id+"F9.imprint","IMPRINT",EDGE,{"derivedFrom":sQuery(id+"F9.wireOp",EDGE,"E179")}),-1.0]])]});
            var Q13;
            Q13=makeQuery(id+"F9.imprint","IMPRINT",FACE,{"disambiguationData":[TD([[makeQuery(id+"F9.imprint","IMPRINT",EDGE,{"derivedFrom":sQuery(id+"F9.wireOp",EDGE,"E178")}),-1.0]])]});
            extrude(context, id + "F10", {"entities" : qUnion([Q0, Q1, Q2, Q3, Q4, Q5, Q6, Q7, Q8, Q9, Q10, Q11, Q12, Q13]), "oppositeDirection" : true, "depth" : 1 / 50.8 * mm});
        }
        {
            var Q0;
            Q0=makeQuery(id+"F9.imprint","IMPRINT",FACE,{"disambiguationData":[TD([[makeQuery(id+"F9.imprint","IMPRINT",EDGE,{"derivedFrom":sQuery(id+"F9.wireOp",EDGE,"E184")}),-1.0]])]});
            var Q1;
            Q1=makeQuery(id+"F9.imprint","IMPRINT",FACE,{"disambiguationData":[TD([[makeQuery(id+"F9.imprint","IMPRINT",EDGE,{"derivedFrom":sQuery(id+"F9.wireOp",EDGE,"E174")}),-1.0]])]});
            var Q2;
            Q2=makeQuery(id+"F9.imprint","IMPRINT",FACE,{"disambiguationData":[TD([[makeQuery(id+"F9.imprint","IMPRINT",EDGE,{"derivedFrom":sQuery(id+"F9.wireOp",EDGE,"E177")}),-1.0]])]});
            var Q3;
            Q3=makeQuery(id+"F9.imprint","IMPRINT",FACE,{"disambiguationData":[TD([[makeQuery(id+"F9.imprint","IMPRINT",EDGE,{"derivedFrom":sQuery(id+"F9.wireOp",EDGE,"E175")}),-1.0]])]});
            var Q4;
            Q4=makeQuery(id+"F9.imprint","IMPRINT",FACE,{"disambiguationData":[TD([[makeQuery(id+"F9.imprint","IMPRINT",EDGE,{"derivedFrom":sQuery(id+"F9.wireOp",EDGE,"E176")}),-1.0]])]});
            var Q5;
            Q5=makeQuery(id+"F9.imprint","IMPRINT",FACE,{"disambiguationData":[TD([[makeQuery(id+"F9.imprint","IMPRINT",EDGE,{"derivedFrom":sQuery(id+"F9.wireOp",EDGE,"E183")}),-1.0]])]});
            var Q6;
            Q6=makeQuery(id+"F9.imprint","IMPRINT",FACE,{"disambiguationData":[TD([[makeQuery(id+"F9.imprint","IMPRINT",EDGE,{"derivedFrom":sQuery(id+"F9.wireOp",EDGE,"E182")}),-1.0]])]});
            var Q7;
            Q7=makeQuery(id+"F9.imprint","IMPRINT",FACE,{"disambiguationData":[TD([[makeQuery(id+"F9.imprint","IMPRINT",EDGE,{"derivedFrom":sQuery(id+"F9.wireOp",EDGE,"E185")}),-1.0]])]});
            var Q8;
            Q8=makeQuery(id+"F9.imprint","IMPRINT",FACE,{"disambiguationData":[TD([[makeQuery(id+"F9.imprint","IMPRINT",EDGE,{"derivedFrom":sQuery(id+"F9.wireOp",EDGE,"E178")}),-1.0]])]});
            var Q9;
            Q9=makeQuery(id+"F9.imprint","IMPRINT",FACE,{"disambiguationData":[TD([[makeQuery(id+"F9.imprint","IMPRINT",EDGE,{"derivedFrom":sQuery(id+"F9.wireOp",EDGE,"E180")}),-1.0]])]});
            var Q10;
            Q10=makeQuery(id+"F9.imprint","IMPRINT",FACE,{"disambiguationData":[TD([[makeQuery(id+"F9.imprint","IMPRINT",EDGE,{"derivedFrom":sQuery(id+"F9.wireOp",EDGE,"E179")}),-1.0]])]});
            var Q11;
            Q11=makeQuery(id+"F9.imprint","IMPRINT",FACE,{"disambiguationData":[TD([[makeQuery(id+"F9.imprint","IMPRINT",EDGE,{"derivedFrom":sQuery(id+"F9.wireOp",EDGE,"E181")}),-1.0]])]});
            extrude(context, id + "F11", {"entities" : qUnion([Q0, Q1, Q2, Q3, Q4, Q5, Q6, Q7, Q8, Q9, Q10, Q11]), "operationType" : NewBodyOperationType.REMOVE, "oppositeDirection" : true, "depth" : 5 * mm});
        }
        {
            var Q0;
            Q0=makeQuery(id+"F9.imprint","IMPRINT",FACE,{"disambiguationData":[TD([[makeQuery(id+"F9.imprint","IMPRINT",EDGE,{"derivedFrom":sQuery(id+"F9.wireOp",EDGE,"E153.bottom")}),1.0]])]});
            var sketch = newSketch(context, id + "F12", { "sketchPlane" : qUnion([Q0])});
            skLineSegment(sketch, "E265", {"start": v(143.73, 159.42) * mm, "end": v(143.73, 111) * mm, "construction": true});
            skLineSegment(sketch, "E266", {"start": v(224.33, 159.42) * mm, "end": v(224.33, 111) * mm, "construction": true});
            skLineSegment(sketch, "E267", {"start": v(224.33, 159.42) * mm, "end": v(143.73, 159.42) * mm, "construction": true});
            skLineSegment(sketch, "E268.bottom", {"start": v(155.73, 150.42) * mm, "end": v(131.73, 150.42) * mm, "construction": true});
            skLineSegment(sketch, "E268.top", {"start": v(155.73, 168.42) * mm, "end": v(131.73, 168.42) * mm, "construction": true});
            skLineSegment(sketch, "E268.left", {"start": v(155.73, 150.42) * mm, "end": v(155.73, 168.42) * mm, "construction": true});
            skLineSegment(sketch, "E268.right", {"start": v(131.73, 150.42) * mm, "end": v(131.73, 168.42) * mm, "construction": true});
            skPoint(sketch, "E268.middle", {"position": v(143.73, 159.42) * mm});
            skLineSegment(sketch, "E269.bottom", {"start": v(236.33, 150.42) * mm, "end": v(212.33, 150.42) * mm, "construction": true});
            skLineSegment(sketch, "E269.top", {"start": v(236.33, 168.42) * mm, "end": v(212.33, 168.42) * mm, "construction": true});
            skLineSegment(sketch, "E269.left", {"start": v(236.33, 150.42) * mm, "end": v(236.33, 168.42) * mm, "construction": true});
            skLineSegment(sketch, "E269.right", {"start": v(212.33, 150.42) * mm, "end": v(212.33, 168.42) * mm, "construction": true});
            skPoint(sketch, "E269.middle", {"position": v(224.33, 159.42) * mm});
            skLineSegment(sketch, "E270.bottom", {"start": v(246.33, 178.42) * mm, "end": v(121.73, 178.42) * mm, "construction": true});
            skLineSegment(sketch, "E270.top", {"start": v(241.33, 140.42) * mm, "end": v(126.73, 140.42) * mm});
            skLineSegment(sketch, "E270.left", {"start": v(246.33, 173.42) * mm, "end": v(246.33, 145.42) * mm});
            skLineSegment(sketch, "E270.right", {"start": v(121.73, 173.42) * mm, "end": v(121.73, 145.42) * mm});
            skPoint(sketch, "E270.middle", {"position": v(184.03, 159.42) * mm});
            skCircle(sketch, "E271", {"center": v(131.73, 168.42) * mm, "radius": 2 * mm});
            skCircle(sketch, "E272", {"center": v(131.73, 150.42) * mm, "radius": 2 * mm});
            skCircle(sketch, "E273", {"center": v(155.73, 168.42) * mm, "radius": 2 * mm});
            skCircle(sketch, "E274", {"center": v(155.73, 150.42) * mm, "radius": 2 * mm});
            skCircle(sketch, "E275", {"center": v(212.33, 150.42) * mm, "radius": 2 * mm});
            skCircle(sketch, "E276", {"center": v(212.33, 168.42) * mm, "radius": 2 * mm});
            skCircle(sketch, "E277", {"center": v(236.33, 168.42) * mm, "radius": 2 * mm});
            skCircle(sketch, "E278", {"center": v(236.33, 150.42) * mm, "radius": 2 * mm});
            skLineSegment(sketch, "E279", {"start": v(159.03, 218.42) * mm, "end": v(209.03, 218.42) * mm});
            skLineSegment(sketch, "E280", {"start": v(121.73, 174.42) * mm, "end": v(246.33, 174.42) * mm, "construction": true});
            skLineSegment(sketch, "E281", {"start": v(121.73, 161.72) * mm, "end": v(246.33, 161.72) * mm, "construction": true});
            skLineSegment(sketch, "E282", {"start": v(184.03, 174.42) * mm, "end": v(184.03, 161.72) * mm, "construction": true});
            skLineSegment(sketch, "E283", {"start": v(184.03, 168.07) * mm, "end": v(192.03, 168.07) * mm, "construction": true});
            skLineSegment(sketch, "E284", {"start": v(184.03, 168.07) * mm, "end": v(176.03, 168.07) * mm, "construction": true});
            skCircle(sketch, "E285", {"center": v(192.03, 168.07) * mm, "radius": 2.5 * mm});
            skCircle(sketch, "E286", {"center": v(176.03, 168.07) * mm, "radius": 2.5 * mm});
            skCircle(sketch, "E287", {"center": v(176.03, 168.07) * mm, "radius": 4.5 * mm});
            skCircle(sketch, "E288", {"center": v(192.03, 168.07) * mm, "radius": 4.5 * mm});
            skLineSegment(sketch, "E289", {"start": v(184.03, 140.42) * mm, "end": v(184.03, 218.42) * mm, "construction": true});
            skLineSegment(sketch, "E290", {"start": v(174.03, 218.42) * mm, "end": v(174.03, 140.42) * mm, "construction": true});
            skLineSegment(sketch, "E291", {"start": v(194.03, 218.42) * mm, "end": v(194.03, 140.42) * mm, "construction": true});
            skLineSegment(sketch, "E292", {"start": v(164.03, 208.42) * mm, "end": v(204.03, 208.42) * mm, "construction": true});
            skLineSegment(sketch, "E293", {"start": v(164.03, 198.42) * mm, "end": v(204.03, 198.42) * mm, "construction": true});
            skLineSegment(sketch, "E294", {"start": v(164.03, 150.42) * mm, "end": v(204.03, 150.42) * mm, "construction": true});
            skLineSegment(sketch, "E295", {"start": v(204.03, 160.42) * mm, "end": v(164.03, 160.42) * mm, "construction": true});
            skCircle(sketch, "E296", {"center": v(174.03, 160.42) * mm, "radius": 2.25 * mm});
            skCircle(sketch, "E297", {"center": v(174.03, 150.42) * mm, "radius": 2.25 * mm});
            skCircle(sketch, "E298", {"center": v(194.03, 150.42) * mm, "radius": 2.25 * mm});
            skCircle(sketch, "E299", {"center": v(194.03, 160.42) * mm, "radius": 2.25 * mm});
            skCircle(sketch, "E300", {"center": v(174.03, 208.42) * mm, "radius": 2.25 * mm});
            skCircle(sketch, "E301", {"center": v(174.03, 198.42) * mm, "radius": 2.25 * mm});
            skCircle(sketch, "E302", {"center": v(194.03, 208.42) * mm, "radius": 2.25 * mm});
            skCircle(sketch, "E303", {"center": v(194.03, 198.42) * mm, "radius": 2.25 * mm});
            skCircle(sketch, "E304", {"center": v(184.03, 208.42) * mm, "radius": 2.25 * mm});
            skCircle(sketch, "E305", {"center": v(184.03, 198.42) * mm, "radius": 2.25 * mm});
            skCircle(sketch, "E306", {"center": v(184.03, 150.42) * mm, "radius": 2.25 * mm});
            skCircle(sketch, "E307", {"center": v(184.03, 160.42) * mm, "radius": 2.25 * mm});
            skPoint(sketch, "E308.visualSharp", {"position": v(126.77, 218.42) * mm});
            skPoint(sketch, "E309.visualSharp", {"position": v(241.3, 218.42) * mm});
            skPoint(sketch, "E310.visualSharp", {"position": v(246.33, 140.42) * mm});
            skArc(sketch, "E310.filletArc", {"start": v(241.33, 140.42) * mm, "mid": v(244.87, 141.89) * mm, "end": v(246.33, 145.42) * mm});
            skPoint(sketch, "E311.visualSharp", {"position": v(121.73, 140.42) * mm});
            skArc(sketch, "E311.filletArc", {"start": v(121.73, 145.42) * mm, "mid": v(123.2, 141.89) * mm, "end": v(126.73, 140.42) * mm});
            skCircle(sketch, "E312", {"center": v(131.73, 168.42) * mm, "radius": 3.5 * mm});
            skCircle(sketch, "E313", {"center": v(131.73, 150.42) * mm, "radius": 3.5 * mm});
            skCircle(sketch, "E314", {"center": v(155.73, 168.42) * mm, "radius": 3.5 * mm});
            skCircle(sketch, "E315", {"center": v(155.73, 150.42) * mm, "radius": 3.5 * mm});
            skCircle(sketch, "E316", {"center": v(212.33, 168.42) * mm, "radius": 3.5 * mm});
            skCircle(sketch, "E317", {"center": v(212.33, 150.42) * mm, "radius": 3.5 * mm});
            skCircle(sketch, "E318", {"center": v(236.33, 150.42) * mm, "radius": 3.5 * mm});
            skCircle(sketch, "E319", {"center": v(236.33, 168.42) * mm, "radius": 3.5 * mm});
            skLineSegment(sketch, "E320", {"start": v(164.03, 188.42) * mm, "end": v(204.03, 188.42) * mm});
            skCircle(sketch, "E321", {"center": v(174.03, 188.42) * mm, "radius": 2.25 * mm});
            skCircle(sketch, "E322", {"center": v(184.03, 188.42) * mm, "radius": 2.25 * mm});
            skCircle(sketch, "E323", {"center": v(194.03, 188.42) * mm, "radius": 2.25 * mm});
            skLineSegment(sketch, "E324", {"start": v(154.03, 213.42) * mm, "end": v(154.03, 183.42) * mm});
            skLineSegment(sketch, "E325", {"start": v(149.03, 178.42) * mm, "end": v(126.73, 178.42) * mm});
            skLineSegment(sketch, "E326", {"start": v(214.03, 213.42) * mm, "end": v(214.03, 183.42) * mm});
            skLineSegment(sketch, "E327", {"start": v(219.03, 178.42) * mm, "end": v(241.33, 178.42) * mm});
            skPoint(sketch, "E328.orphan", {"position": v(231.37, 218.42) * mm});
            skPoint(sketch, "E329.visualSharp", {"position": v(154.03, 218.42) * mm});
            skArc(sketch, "E329.filletArc", {"start": v(159.03, 218.42) * mm, "mid": v(155.5, 216.96) * mm, "end": v(154.03, 213.42) * mm});
            skPoint(sketch, "E330.visualSharp", {"position": v(214.03, 218.42) * mm});
            skArc(sketch, "E330.filletArc", {"start": v(214.03, 213.42) * mm, "mid": v(212.57, 216.96) * mm, "end": v(209.03, 218.42) * mm});
            skPoint(sketch, "E331.visualSharp", {"position": v(121.73, 178.42) * mm});
            skArc(sketch, "E331.filletArc", {"start": v(126.73, 178.42) * mm, "mid": v(123.2, 176.96) * mm, "end": v(121.73, 173.42) * mm});
            skPoint(sketch, "E332.visualSharp", {"position": v(154.03, 178.42) * mm});
            skArc(sketch, "E332.filletArc", {"start": v(149.03, 178.42) * mm, "mid": v(152.57, 179.89) * mm, "end": v(154.03, 183.42) * mm});
            skPoint(sketch, "E333.visualSharp", {"position": v(214.03, 178.42) * mm});
            skArc(sketch, "E333.filletArc", {"start": v(214.03, 183.42) * mm, "mid": v(215.5, 179.89) * mm, "end": v(219.03, 178.42) * mm});
            skPoint(sketch, "E334.visualSharp", {"position": v(246.33, 178.42) * mm});
            skArc(sketch, "E334.filletArc", {"start": v(246.33, 173.42) * mm, "mid": v(244.87, 176.96) * mm, "end": v(241.33, 178.42) * mm});
            skLineSegment(sketch, "E335", {"start": v(143.73, 159.42) * mm, "end": v(143.73, 265.88) * mm, "construction": true});
            skLineSegment(sketch, "E336", {"start": v(224.33, 159.42) * mm, "end": v(224.33, 265.88) * mm, "construction": true});
            skLineSegment(sketch, "E337", {"start": v(126.73, 265.88) * mm, "end": v(160.73, 265.88) * mm, "construction": true});
            skLineSegment(sketch, "E338", {"start": v(207.33, 265.88) * mm, "end": v(241.33, 265.88) * mm, "construction": true});
            skPoint(sketch, "E339", {"position": v(143.73, 265.88) * mm});
            skPoint(sketch, "E340", {"position": v(224.33, 265.88) * mm});
            skLineSegment(sketch, "E341", {"start": v(164.03, 218.42) * mm, "end": v(164.03, 140.42) * mm, "construction": true});
            skLineSegment(sketch, "E342", {"start": v(204.03, 218.42) * mm, "end": v(204.03, 140.42) * mm, "construction": true});
            skCircle(sketch, "E343", {"center": v(164.03, 208.42) * mm, "radius": 2.25 * mm});
            skCircle(sketch, "E344", {"center": v(164.03, 198.42) * mm, "radius": 2.25 * mm});
            skCircle(sketch, "E345", {"center": v(164.03, 188.42) * mm, "radius": 2.25 * mm});
            skCircle(sketch, "E346", {"center": v(164.03, 160.42) * mm, "radius": 2.25 * mm});
            skCircle(sketch, "E347", {"center": v(204.03, 208.42) * mm, "radius": 2.25 * mm});
            skCircle(sketch, "E348", {"center": v(204.03, 198.42) * mm, "radius": 2.25 * mm});
            skCircle(sketch, "E349", {"center": v(204.03, 188.42) * mm, "radius": 2.25 * mm});
            skCircle(sketch, "E350", {"center": v(204.03, 160.42) * mm, "radius": 2.25 * mm});
            skCircle(sketch, "E351", {"center": v(164.03, 150.42) * mm, "radius": 2.25 * mm});
            skCircle(sketch, "E352", {"center": v(204.03, 150.42) * mm, "radius": 2.25 * mm});
            skSolve(sketch);
        }
        {
            var Q0;
            Q0=makeQuery(id+"F12.imprint","IMPRINT",FACE,{"disambiguationData":[TD([[makeQuery(id+"F12.imprint","IMPRINT",EDGE,{"derivedFrom":sQuery(id+"F12.wireOp",EDGE,"E286")}),-1.0]])]});
            var Q1;
            Q1=makeQuery(id+"F12.imprint","IMPRINT",FACE,{"disambiguationData":[TD([[makeQuery(id+"F12.imprint","IMPRINT",EDGE,{"derivedFrom":sQuery(id+"F12.wireOp",EDGE,"E285")}),-1.0]])]});
            var Q2;
            Q2=makeQuery(id+"F12.imprint","IMPRINT",FACE,{"disambiguationData":[TD([[makeQuery(id+"F12.imprint","IMPRINT",EDGE,{"derivedFrom":sQuery(id+"F12.wireOp",EDGE,"E271")}),-1.0]])]});
            var Q3;
            Q3=makeQuery(id+"F12.imprint","IMPRINT",FACE,{"disambiguationData":[TD([[makeQuery(id+"F12.imprint","IMPRINT",EDGE,{"derivedFrom":sQuery(id+"F12.wireOp",EDGE,"E272")}),-1.0]])]});
            var Q4;
            Q4=makeQuery(id+"F12.imprint","IMPRINT",FACE,{"disambiguationData":[TD([[makeQuery(id+"F12.imprint","IMPRINT",EDGE,{"derivedFrom":sQuery(id+"F12.wireOp",EDGE,"E273")}),-1.0]])]});
            var Q5;
            Q5=makeQuery(id+"F12.imprint","IMPRINT",FACE,{"disambiguationData":[TD([[makeQuery(id+"F12.imprint","IMPRINT",EDGE,{"derivedFrom":sQuery(id+"F12.wireOp",EDGE,"E274")}),-1.0]])]});
            var Q6;
            Q6=makeQuery(id+"F12.imprint","IMPRINT",FACE,{"disambiguationData":[TD([[makeQuery(id+"F12.imprint","IMPRINT",EDGE,{"derivedFrom":sQuery(id+"F12.wireOp",EDGE,"E276")}),-1.0]])]});
            var Q7;
            Q7=makeQuery(id+"F12.imprint","IMPRINT",FACE,{"disambiguationData":[TD([[makeQuery(id+"F12.imprint","IMPRINT",EDGE,{"derivedFrom":sQuery(id+"F12.wireOp",EDGE,"E275")}),-1.0]])]});
            var Q8;
            Q8=makeQuery(id+"F12.imprint","IMPRINT",FACE,{"disambiguationData":[TD([[makeQuery(id+"F12.imprint","IMPRINT",EDGE,{"derivedFrom":sQuery(id+"F12.wireOp",EDGE,"E277")}),-1.0]])]});
            var Q9;
            Q9=makeQuery(id+"F12.imprint","IMPRINT",FACE,{"disambiguationData":[TD([[makeQuery(id+"F12.imprint","IMPRINT",EDGE,{"derivedFrom":sQuery(id+"F12.wireOp",EDGE,"E270.top")}),-1.0]])]});
            var Q10;
            Q10=makeQuery(id+"F12.imprint","IMPRINT",FACE,{"disambiguationData":[TD([[makeQuery(id+"F12.imprint","IMPRINT",EDGE,{"derivedFrom":sQuery(id+"F12.wireOp",EDGE,"E278")}),-1.0]])]});
            extrude(context, id + "F13", {"entities" : qUnion([Q0, Q1, Q2, Q3, Q4, Q5, Q6, Q7, Q8, Q9, Q10]), "oppositeDirection" : true, "depth" : 12.7 * mm});
        }
        {
            var Q0;
            Q0=makeQuery(id+"F12.imprint","IMPRINT",FACE,{"disambiguationData":[TD([[makeQuery(id+"F12.imprint","IMPRINT",EDGE,{"derivedFrom":sQuery(id+"F12.wireOp",EDGE,"E273")}),-1.0]])]});
            var Q1;
            Q1=makeQuery(id+"F12.imprint","IMPRINT",FACE,{"disambiguationData":[TD([[makeQuery(id+"F12.imprint","IMPRINT",EDGE,{"derivedFrom":sQuery(id+"F12.wireOp",EDGE,"E271")}),-1.0]])]});
            var Q2;
            Q2=makeQuery(id+"F12.imprint","IMPRINT",FACE,{"disambiguationData":[TD([[makeQuery(id+"F12.imprint","IMPRINT",EDGE,{"derivedFrom":sQuery(id+"F12.wireOp",EDGE,"E272")}),-1.0]])]});
            var Q3;
            Q3=makeQuery(id+"F12.imprint","IMPRINT",FACE,{"disambiguationData":[TD([[makeQuery(id+"F12.imprint","IMPRINT",EDGE,{"derivedFrom":sQuery(id+"F12.wireOp",EDGE,"E274")}),-1.0]])]});
            var Q4;
            Q4=makeQuery(id+"F12.imprint","IMPRINT",FACE,{"disambiguationData":[TD([[makeQuery(id+"F12.imprint","IMPRINT",EDGE,{"derivedFrom":sQuery(id+"F12.wireOp",EDGE,"E286")}),-1.0]])]});
            var Q5;
            Q5=makeQuery(id+"F12.imprint","IMPRINT",FACE,{"disambiguationData":[TD([[makeQuery(id+"F12.imprint","IMPRINT",EDGE,{"derivedFrom":sQuery(id+"F12.wireOp",EDGE,"E285")}),-1.0]])]});
            var Q6;
            Q6=makeQuery(id+"F12.imprint","IMPRINT",FACE,{"disambiguationData":[TD([[makeQuery(id+"F12.imprint","IMPRINT",EDGE,{"derivedFrom":sQuery(id+"F12.wireOp",EDGE,"E276")}),-1.0]])]});
            var Q7;
            Q7=makeQuery(id+"F12.imprint","IMPRINT",FACE,{"disambiguationData":[TD([[makeQuery(id+"F12.imprint","IMPRINT",EDGE,{"derivedFrom":sQuery(id+"F12.wireOp",EDGE,"E277")}),-1.0]])]});
            var Q8;
            Q8=makeQuery(id+"F12.imprint","IMPRINT",FACE,{"disambiguationData":[TD([[makeQuery(id+"F12.imprint","IMPRINT",EDGE,{"derivedFrom":sQuery(id+"F12.wireOp",EDGE,"E278")}),-1.0]])]});
            var Q9;
            Q9=makeQuery(id+"F12.imprint","IMPRINT",FACE,{"disambiguationData":[TD([[makeQuery(id+"F12.imprint","IMPRINT",EDGE,{"derivedFrom":sQuery(id+"F12.wireOp",EDGE,"E275")}),-1.0]])]});
            extrude(context, id + "F14", {"entities" : qUnion([Q0, Q1, Q2, Q3, Q4, Q5, Q6, Q7, Q8, Q9]), "operationType" : NewBodyOperationType.REMOVE, "oppositeDirection" : true, "depth" : 5 * mm});
        }
        {
            var Q0;
            Q0=qCreatedBy(makeId("Top.planeOp"),FACE);
            var sketch = newSketch(context, id + "F15", { "sketchPlane" : qUnion([Q0])});
            skLineSegment(sketch, "E353.bottom", {"start": v(162.53, 340.38) * mm, "end": v(205.53, 340.38) * mm});
            skLineSegment(sketch, "E353.top", {"start": v(162.53, 327.68) * mm, "end": v(205.53, 327.68) * mm});
            skLineSegment(sketch, "E353.left", {"start": v(162.53, 340.38) * mm, "end": v(162.53, 327.68) * mm});
            skLineSegment(sketch, "E353.right", {"start": v(205.53, 340.38) * mm, "end": v(205.53, 327.68) * mm});
            skPoint(sketch, "E354.0", {"position": v(176.03, 168.07) * mm});
            skPoint(sketch, "E354.1", {"position": v(192.03, 168.07) * mm});
            skLineSegment(sketch, "E355", {"start": v(176.03, 168.07) * mm, "end": v(192.03, 168.07) * mm, "construction": true});
            skLineSegment(sketch, "E356", {"start": v(176.03, 334.03) * mm, "end": v(192.03, 334.03) * mm, "construction": true});
            skLineSegment(sketch, "E357", {"start": v(176.03, 334.03) * mm, "end": v(162.53, 334.03) * mm, "construction": true});
            skPoint(sketch, "E358.endSnap0", {"position": v(205.53, 334.03) * mm});
            skLineSegment(sketch, "E359", {"start": v(192.03, 334.03) * mm, "end": v(205.53, 334.03) * mm, "construction": true});
            skCircle(sketch, "E360", {"center": v(176.03, 334.03) * mm, "radius": 2.25 * mm});
            skCircle(sketch, "E361", {"center": v(192.03, 334.03) * mm, "radius": 2.25 * mm});
            skLineSegment(sketch, "E362", {"start": v(162.53, 353.08) * mm, "end": v(205.53, 353.08) * mm});
            skLineSegment(sketch, "E363", {"start": v(205.53, 353.08) * mm, "end": v(205.53, 340.38) * mm});
            skLineSegment(sketch, "E364", {"start": v(162.53, 340.38) * mm, "end": v(162.53, 353.08) * mm});
            skLineSegment(sketch, "E365", {"start": v(162.53, 327.68) * mm, "end": v(162.53, 314.98) * mm});
            skLineSegment(sketch, "E366", {"start": v(162.53, 314.98) * mm, "end": v(205.53, 314.98) * mm});
            skLineSegment(sketch, "E367", {"start": v(205.53, 314.98) * mm, "end": v(205.53, 327.68) * mm});
            skLineSegment(sketch, "E368", {"start": v(176.03, 168.07) * mm, "end": v(176.03, 334.03) * mm});
            skLineSegment(sketch, "E369", {"start": v(192.03, 168.07) * mm, "end": v(192.03, 334.03) * mm});
            skSolve(sketch);
        }
        {
            var Q0;
            Q0=makeQuery(id+"F15.imprint","IMPRINT",FACE,{"disambiguationData":[TD([[makeQuery(id+"F15.imprint","IMPRINT",EDGE,{"derivedFrom":sQuery(id+"F15.wireOp",EDGE,"E353.bottom")}),1.0]])]});
            var Q1;
            Q1=makeQuery(id+"F15.imprint","IMPRINT",FACE,{"disambiguationData":[TD([[makeQuery(id+"F15.imprint","IMPRINT",EDGE,{"derivedFrom":sQuery(id+"F15.wireOp",EDGE,"E353.bottom")}),-1.0]])]});
            var Q2;
            Q2=makeQuery(id+"F15.imprint","IMPRINT",FACE,{"disambiguationData":[TD([[makeQuery(id+"F15.imprint","IMPRINT",EDGE,{"derivedFrom":sQuery(id+"F15.wireOp",EDGE,"E353.top")}),-1.0]])]});
            extrude(context, id + "F16", {"entities" : qUnion([Q0, Q1, Q2]), "oppositeDirection" : true, "depth" : 1 / 50.8 * mm});
        }
        {
            var Q0;
            Q0=makeQuery(id+"F15.imprint","IMPRINT",FACE,{"disambiguationData":[TD([[makeQuery(id+"F15.imprint","IMPRINT",EDGE,{"derivedFrom":sQuery(id+"F15.wireOp",EDGE,"E353.bottom")}),-1.0]])]});
            extrude(context, id + "F17", {"entities" : qUnion([Q0]), "operationType" : NewBodyOperationType.REMOVE, "oppositeDirection" : true, "depth" : 1 / 101.6 * mm});
        }
        {
            var Q0;
            Q0=qCreatedBy(makeId("Top.planeOp"),FACE);
            var sketch = newSketch(context, id + "F18", { "sketchPlane" : qUnion([Q0])});
            skPoint(sketch, "E370.0", {"position": v(176.03, 334.03) * mm});
            skPoint(sketch, "E370.1", {"position": v(192.03, 334.03) * mm});
            skLineSegment(sketch, "E371", {"start": v(176.03, 334.03) * mm, "end": v(176.03, 363.08) * mm, "construction": true});
            skLineSegment(sketch, "E372", {"start": v(192.03, 334.03) * mm, "end": v(192.03, 363.08) * mm, "construction": true});
            skPoint(sketch, "E373.0", {"position": v(162.53, 353.08) * mm});
            skPoint(sketch, "E373.1", {"position": v(205.53, 353.08) * mm});
            skLineSegment(sketch, "E374", {"start": v(162.53, 353.08) * mm, "end": v(162.53, 363.08) * mm, "construction": true});
            skLineSegment(sketch, "E375", {"start": v(162.53, 363.08) * mm, "end": v(205.53, 363.08) * mm});
            skLineSegment(sketch, "E376", {"start": v(205.53, 363.08) * mm, "end": v(205.53, 353.08) * mm, "construction": true});
            skLineSegment(sketch, "E377", {"start": v(162.53, 363.08) * mm, "end": v(162.53, 406.08) * mm});
            skLineSegment(sketch, "E378", {"start": v(162.53, 406.08) * mm, "end": v(205.53, 406.08) * mm, "construction": true});
            skLineSegment(sketch, "E379", {"start": v(205.53, 406.08) * mm, "end": v(205.53, 363.08) * mm});
            skLineSegment(sketch, "E380", {"start": v(184.03, 406.08) * mm, "end": v(184.03, 363.08) * mm, "construction": true});
            skPoint(sketch, "E381", {"position": v(184.03, 384.58) * mm});
            skLineSegment(sketch, "E382.bottom", {"start": v(199.53, 369.08) * mm, "end": v(168.53, 369.08) * mm, "construction": true});
            skLineSegment(sketch, "E382.top", {"start": v(199.53, 400.08) * mm, "end": v(168.53, 400.08) * mm, "construction": true});
            skLineSegment(sketch, "E382.left", {"start": v(199.53, 369.08) * mm, "end": v(199.53, 400.08) * mm, "construction": true});
            skLineSegment(sketch, "E382.right", {"start": v(168.53, 369.08) * mm, "end": v(168.53, 400.08) * mm, "construction": true});
            skCircle(sketch, "E383", {"center": v(184.03, 384.58) * mm, "radius": 11.5 * mm});
            skCircle(sketch, "E384", {"center": v(168.53, 369.08) * mm, "radius": 1.75 * mm});
            skCircle(sketch, "E385", {"center": v(168.53, 400.08) * mm, "radius": 1.75 * mm});
            skCircle(sketch, "E386", {"center": v(199.53, 400.08) * mm, "radius": 1.75 * mm});
            skCircle(sketch, "E387", {"center": v(199.53, 369.08) * mm, "radius": 1.75 * mm});
            skCircle(sketch, "E388", {"center": v(168.53, 400.08) * mm, "radius": 2.75 * mm});
            skCircle(sketch, "E389", {"center": v(199.53, 400.08) * mm, "radius": 2.75 * mm});
            skCircle(sketch, "E390", {"center": v(199.53, 369.08) * mm, "radius": 2.75 * mm});
            skCircle(sketch, "E391", {"center": v(168.53, 369.08) * mm, "radius": 2.75 * mm});
            skLineSegment(sketch, "E392", {"start": v(162.53, 406.08) * mm, "end": v(162.53, 416.08) * mm});
            skLineSegment(sketch, "E393", {"start": v(162.53, 416.08) * mm, "end": v(205.53, 416.08) * mm});
            skLineSegment(sketch, "E394", {"start": v(205.53, 416.08) * mm, "end": v(205.53, 406.08) * mm});
            skSolve(sketch);
        }
        {
            var Q0;
            Q0=makeQuery(id+"F18.imprint","IMPRINT",FACE,{"disambiguationData":[TD([[makeQuery(id+"F18.imprint","IMPRINT",EDGE,{"derivedFrom":sQuery(id+"F18.wireOp",EDGE,"E375")}),1.0]])]});
            var Q1;
            Q1=makeQuery(id+"F18.imprint","IMPRINT",FACE,{"disambiguationData":[TD([[makeQuery(id+"F18.imprint","IMPRINT",EDGE,{"derivedFrom":sQuery(id+"F18.wireOp",EDGE,"E384")}),-1.0]])]});
            var Q2;
            Q2=makeQuery(id+"F18.imprint","IMPRINT",FACE,{"disambiguationData":[TD([[makeQuery(id+"F18.imprint","IMPRINT",EDGE,{"derivedFrom":sQuery(id+"F18.wireOp",EDGE,"E385")}),-1.0]])]});
            var Q3;
            Q3=makeQuery(id+"F18.imprint","IMPRINT",FACE,{"disambiguationData":[TD([[makeQuery(id+"F18.imprint","IMPRINT",EDGE,{"derivedFrom":sQuery(id+"F18.wireOp",EDGE,"E386")}),-1.0]])]});
            var Q4;
            Q4=makeQuery(id+"F18.imprint","IMPRINT",FACE,{"disambiguationData":[TD([[makeQuery(id+"F18.imprint","IMPRINT",EDGE,{"derivedFrom":sQuery(id+"F18.wireOp",EDGE,"E387")}),-1.0]])]});
            extrude(context, id + "F19", {"entities" : qUnion([Q0, Q1, Q2, Q3, Q4]), "oppositeDirection" : true, "depth" : 1 / 50.8 * mm});
        }
        {
            var Q0;
            Q0=makeQuery(id+"F18.imprint","IMPRINT",FACE,{"disambiguationData":[TD([[makeQuery(id+"F18.imprint","IMPRINT",EDGE,{"derivedFrom":sQuery(id+"F18.wireOp",EDGE,"E385")}),-1.0]])]});
            var Q1;
            Q1=makeQuery(id+"F18.imprint","IMPRINT",FACE,{"disambiguationData":[TD([[makeQuery(id+"F18.imprint","IMPRINT",EDGE,{"derivedFrom":sQuery(id+"F18.wireOp",EDGE,"E384")}),-1.0]])]});
            var Q2;
            Q2=makeQuery(id+"F18.imprint","IMPRINT",FACE,{"disambiguationData":[TD([[makeQuery(id+"F18.imprint","IMPRINT",EDGE,{"derivedFrom":sQuery(id+"F18.wireOp",EDGE,"E387")}),-1.0]])]});
            var Q3;
            Q3=makeQuery(id+"F18.imprint","IMPRINT",FACE,{"disambiguationData":[TD([[makeQuery(id+"F18.imprint","IMPRINT",EDGE,{"derivedFrom":sQuery(id+"F18.wireOp",EDGE,"E386")}),-1.0]])]});
            extrude(context, id + "F20", {"entities" : qUnion([Q0, Q1, Q2, Q3]), "operationType" : NewBodyOperationType.REMOVE, "oppositeDirection" : true, "depth" : 5 * mm});
        }
        {
            var Q0;
            Q0=qCreatedBy(makeId("Top.planeOp"),FACE);
            var sketch = newSketch(context, id + "F21", { "sketchPlane" : qUnion([Q0])});
            skPoint(sketch, "E395.0", {"position": v(205.53, 334.03) * mm});
            skLineSegment(sketch, "E396", {"start": v(205.53, 334.03) * mm, "end": v(240.07, 334.03) * mm});
            skLineSegment(sketch, "E397", {"start": v(240.07, 353.08) * mm, "end": v(240.07, 314.98) * mm});
            skLineSegment(sketch, "E398", {"start": v(240.07, 314.98) * mm, "end": v(280.07, 314.98) * mm});
            skLineSegment(sketch, "E399", {"start": v(280.07, 314.98) * mm, "end": v(280.07, 353.08) * mm});
            skLineSegment(sketch, "E400", {"start": v(280.07, 353.08) * mm, "end": v(240.07, 353.08) * mm});
            skLineSegment(sketch, "E401", {"start": v(240.07, 340.38) * mm, "end": v(280.07, 340.38) * mm});
            skLineSegment(sketch, "E402", {"start": v(280.07, 327.68) * mm, "end": v(240.07, 327.68) * mm});
            skPoint(sketch, "E403", {"position": v(240.07, 334.03) * mm});
            skLineSegment(sketch, "E404", {"start": v(252.07, 314.98) * mm, "end": v(252.07, 353.08) * mm, "construction": true});
            skLineSegment(sketch, "E405", {"start": v(268.07, 353.08) * mm, "end": v(268.07, 314.98) * mm, "construction": true});
            skLineSegment(sketch, "E406", {"start": v(240.07, 334.03) * mm, "end": v(280.07, 334.03) * mm, "construction": true});
            skPoint(sketch, "E407", {"position": v(252.07, 334.03) * mm});
            skPoint(sketch, "E408", {"position": v(268.07, 334.03) * mm});
            skPoint(sketch, "E409", {"position": v(260.07, 334.03) * mm});
            skCircle(sketch, "E410", {"center": v(252.07, 334.03) * mm, "radius": 2.25 * mm});
            skCircle(sketch, "E411", {"center": v(268.07, 334.03) * mm, "radius": 2.25 * mm});
            skSolve(sketch);
        }
        {
            var Q0;
            Q0=qCreatedBy(makeId("Top.planeOp"),FACE);
            var sketch = newSketch(context, id + "F22", { "sketchPlane" : qUnion([Q0])});
            skLineSegment(sketch, "E412.bottom", {"start": v(240.07, 378.1) * mm, "end": v(280.07, 378.1) * mm});
            skLineSegment(sketch, "E412.top", {"start": v(240.07, 418.1) * mm, "end": v(280.07, 418.1) * mm, "construction": true});
            skLineSegment(sketch, "E412.left", {"start": v(240.07, 378.1) * mm, "end": v(240.07, 418.1) * mm});
            skLineSegment(sketch, "E412.right", {"start": v(280.07, 378.1) * mm, "end": v(280.07, 418.1) * mm});
            skLineSegment(sketch, "E413", {"start": v(240.07, 378.1) * mm, "end": v(240.07, 353.08) * mm});
            skPoint(sketch, "E414.0", {"position": v(240.07, 353.08) * mm});
            skPoint(sketch, "E415.0", {"position": v(280.07, 353.08) * mm});
            skLineSegment(sketch, "E416", {"start": v(280.07, 378.1) * mm, "end": v(280.07, 353.08) * mm});
            skLineSegment(sketch, "E417", {"start": v(240.07, 398.1) * mm, "end": v(280.07, 398.1) * mm, "construction": true});
            skPoint(sketch, "E418", {"position": v(260.07, 398.1) * mm});
            skLineSegment(sketch, "E419.bottom", {"start": v(271.57, 386.6) * mm, "end": v(248.57, 386.6) * mm, "construction": true});
            skLineSegment(sketch, "E419.top", {"start": v(271.57, 409.6) * mm, "end": v(248.57, 409.6) * mm, "construction": true});
            skLineSegment(sketch, "E419.left", {"start": v(271.57, 386.6) * mm, "end": v(271.57, 409.6) * mm, "construction": true});
            skLineSegment(sketch, "E419.right", {"start": v(248.57, 386.6) * mm, "end": v(248.57, 409.6) * mm, "construction": true});
            skCircle(sketch, "E420", {"center": v(260.07, 398.1) * mm, "radius": 11 * mm});
            skCircle(sketch, "E421", {"center": v(248.57, 409.6) * mm, "radius": 1.75 * mm});
            skCircle(sketch, "E422", {"center": v(271.57, 409.6) * mm, "radius": 1.75 * mm});
            skCircle(sketch, "E423", {"center": v(271.57, 386.6) * mm, "radius": 1.75 * mm});
            skCircle(sketch, "E424", {"center": v(248.57, 386.6) * mm, "radius": 1.75 * mm});
            skLineSegment(sketch, "E425", {"start": v(240.07, 418.1) * mm, "end": v(240.07, 428.1) * mm});
            skLineSegment(sketch, "E426", {"start": v(240.07, 428.1) * mm, "end": v(280.07, 428.1) * mm});
            skLineSegment(sketch, "E427", {"start": v(280.07, 428.1) * mm, "end": v(280.07, 418.1) * mm});
            skSolve(sketch);
        }
        {
            var Q0;
            Q0 = qSketchRegion(id + "F21", true);
            extrude(context, id + "F23", {"entities" : qUnion([Q0]), "oppositeDirection" : true, "depth" : 1 / 50.8 * mm});
        }
        {
            var Q0;
            {var subQ0=sQuery(id+"F21.wireOp",EDGE,"E401");Q0=makeQuery(id+"F21.imprint","IMPRINT",FACE,{"disambiguationData":[TD([[makeQuery(id+"F21.imprint","IMPRINT",EDGE,{"derivedFrom":subQ0}),-1.0]])]});}
            extrude(context, id + "F24", {"entities" : qUnion([Q0]), "operationType" : NewBodyOperationType.REMOVE, "oppositeDirection" : true, "depth" : 1 / 101.6 * mm});
        }
        {
            var Q0;
            Q0=makeQuery(id+"F22.imprint","IMPRINT",FACE,{"disambiguationData":[TD([[makeQuery(id+"F22.imprint","IMPRINT",EDGE,{"derivedFrom":sQuery(id+"F22.wireOp",EDGE,"E412.bottom")}),1.0]])]});
            extrude(context, id + "F25", {"entities" : qUnion([Q0]), "oppositeDirection" : true, "depth" : 1 / 50.8 * mm});
        }
    });
